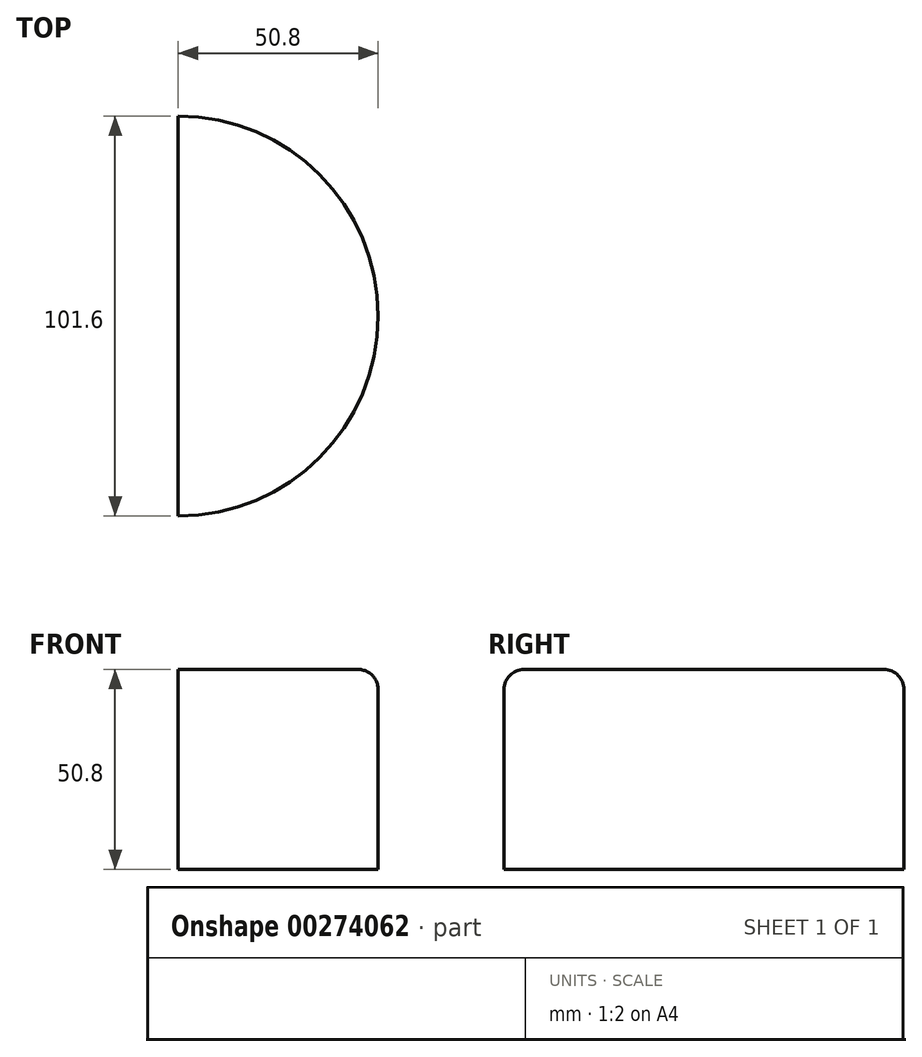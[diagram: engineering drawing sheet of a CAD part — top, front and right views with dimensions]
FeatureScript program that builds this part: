
annotation { "Feature Type Name" : "Feature", "Feature Type Description" : "" }
export const myFeature = defineFeature(function(context is Context, id is Id, definition is map)
    precondition{}
    {
        {
            var Q0;
            Q0=qCreatedBy(makeId("Top.planeOp"),FACE);
            var sketch = newSketch(context, id + "F0", { "sketchPlane" : qUnion([Q0])});
            skCircle(sketch, "E0", {"center": v(0, 0) * mm, "radius": 50.8 * mm});
            skLineSegment(sketch, "E1", {"start": v(0, 50.8) * mm, "end": v(0, -50.8) * mm});
            skSolve(sketch);
        }
        {
            var Q0;
            {var subQ0=sQuery(id+"F0.wireOp",EDGE,"E1");Q0=makeQuery(id+"F0.imprint","IMPRINT",FACE,{"disambiguationData":[TD([[makeQuery(id+"F0.imprint","IMPRINT",EDGE,{"derivedFrom":subQ0}),1.0]])]});}
            extrude(context, id + "F1", {"entities" : qUnion([Q0]), "endBound" : BoundingType.SYMMETRIC, "depth" : 50.8 * mm});
        }
        {
            var Q0;
            Q0=makeQuery(id+"F1.opExtrude","CAP_EDGE",EDGE,{"disambiguationData":[OSD([sQuery(id+"F0.wireOp",EDGE,"E0")])],"isStart":false});
            fillet(context, id + "F2", {"entities" : qUnion([Q0]), "radius" : 5.08 * mm, "tangentPropagation" : true, "allowEdgeOverflow" : false});
        }
    });
